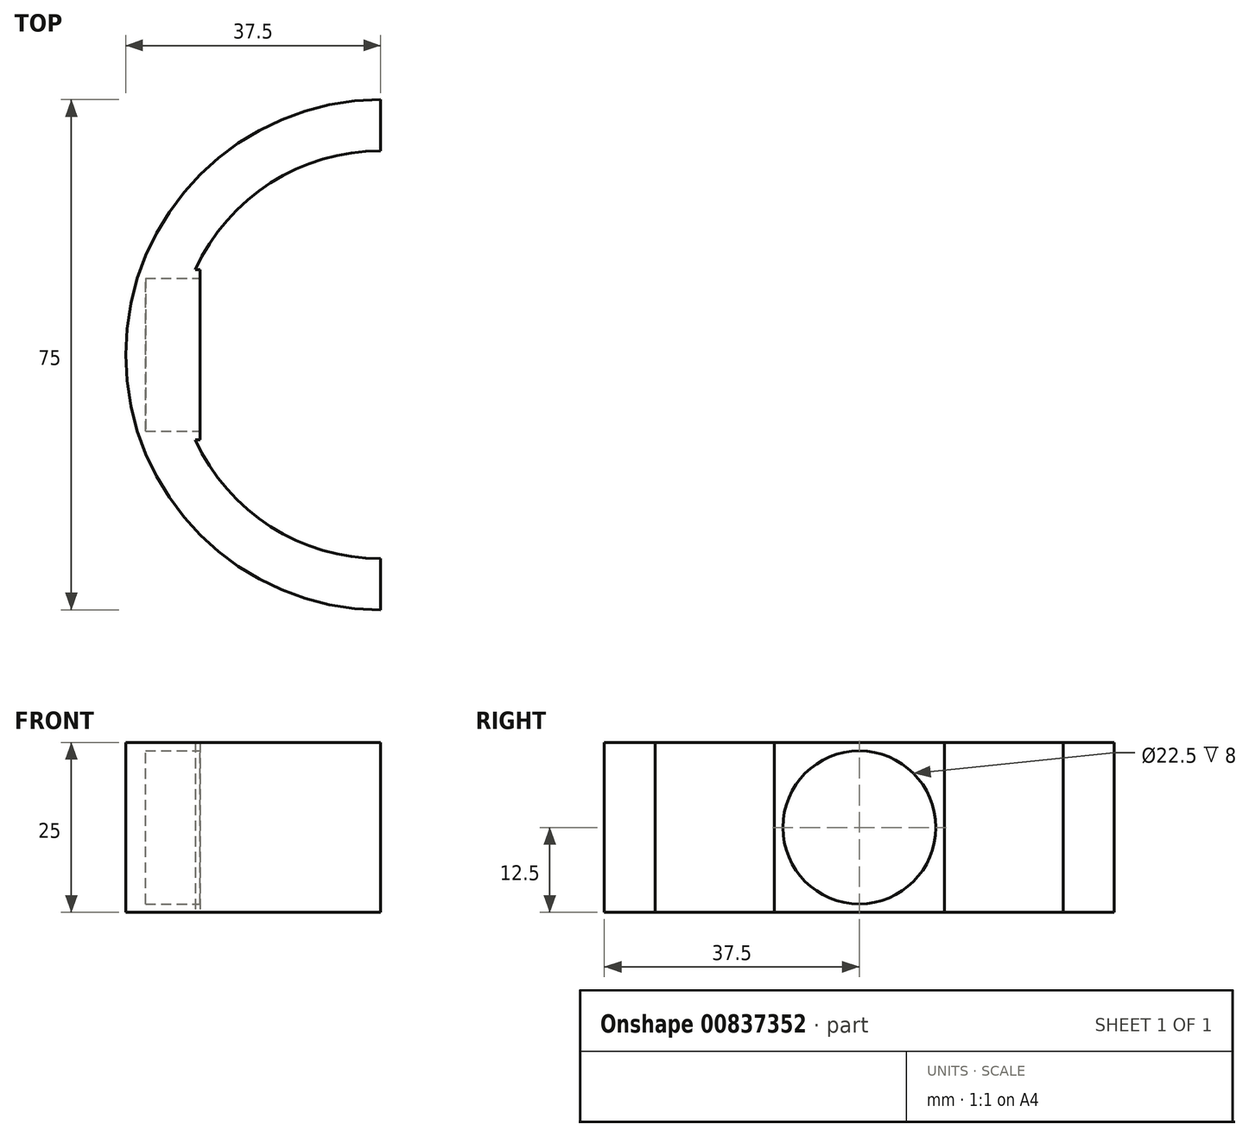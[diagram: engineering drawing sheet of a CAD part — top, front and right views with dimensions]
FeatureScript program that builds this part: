
annotation { "Feature Type Name" : "Feature", "Feature Type Description" : "" }
export const myFeature = defineFeature(function(context is Context, id is Id, definition is map)
    precondition{}
    {
        {
            var Q0;
            Q0=qCreatedBy(makeId("Top.planeOp"),FACE);
            var sketch = newSketch(context, id + "F0", { "sketchPlane" : qUnion([Q0])});
            skArc(sketch, "E0", {"start": v(-27.27, -12.5) * mm, "mid": v(-16.2, -25.25) * mm, "end": v(0, -30) * mm});
            skArc(sketch, "E1", {"start": v(-37.5, 0) * mm, "mid": v(-26.52, -26.52) * mm, "end": v(0, -37.5) * mm});
            skLineSegment(sketch, "E2", {"start": v(-37.5, 0) * mm, "end": v(-26.6, 0) * mm, "construction": true});
            skPoint(sketch, "E2.endSnap0", {"position": v(-26.6, 0) * mm});
            skLineSegment(sketch, "E3", {"start": v(-26.6, -12.5) * mm, "end": v(-27.27, -12.5) * mm});
            skLineSegment(sketch, "E4", {"start": v(0, -30) * mm, "end": v(0, -37.5) * mm});
            skLineSegment(sketch, "E5", {"start": v(-26.6, 0) * mm, "end": v(-26.6, -12.5) * mm});
            skLineSegment(sketch, "E6.MirrorCS", {"start": v(-26.6, 12.5) * mm, "end": v(-27.27, 12.5) * mm});
            skLineSegment(sketch, "E7.MirrorCS", {"start": v(0, 30) * mm, "end": v(0, 37.5) * mm});
            skArc(sketch, "E8.MirrorCS", {"start": v(-37.5, 0) * mm, "mid": v(-26.52, 26.52) * mm, "end": v(0, 37.5) * mm});
            skArc(sketch, "E9.MirrorCS", {"start": v(-27.27, 12.5) * mm, "mid": v(-16.2, 25.25) * mm, "end": v(0, 30) * mm});
            skLineSegment(sketch, "E10.MirrorCS", {"start": v(-26.6, 0) * mm, "end": v(-26.6, 12.5) * mm});
            skSolve(sketch);
        }
        {
            var Q0;
            Q0=makeQuery(id+"F0.imprint","IMPRINT",FACE,{"disambiguationData":[TD([[makeQuery(id+"F0.imprint","IMPRINT",EDGE,{"derivedFrom":sQuery(id+"F0.wireOp",EDGE,"E0")}),-1.0]])]});
            extrude(context, id + "F1", {"entities" : qUnion([Q0]), "depth" : 25 * mm, "offsetDistance" : 25 * mm});
        }
        {
            var Q0;
            Q0=makeQuery(id+"F1.opExtrude","SWEPT_FACE",FACE,{"disambiguationData":[OSD([sQuery(id+"F0.wireOp",EDGE,"E5"),sQuery(id+"F0.wireOp",EDGE,"E10.MirrorCS")])]});
            var sketch = newSketch(context, id + "F2", { "sketchPlane" : qUnion([Q0])});
            skLineSegment(sketch, "E11", {"start": v(-12.5, 25) * mm, "end": v(12.5, 0) * mm, "construction": true});
            skLineSegment(sketch, "E12", {"start": v(-12.5, 0) * mm, "end": v(12.5, 25) * mm, "construction": true});
            skCircle(sketch, "E13", {"center": v(0, 12.5) * mm, "radius": 11.25 * mm});
            skSolve(sketch);
        }
        {
            var Q0;
            Q0=makeQuery(id+"F2.imprint","IMPRINT",FACE,{"disambiguationData":[TD([[makeQuery(id+"F2.imprint","IMPRINT",EDGE,{"derivedFrom":sQuery(id+"F2.wireOp",EDGE,"E13")}),1.0]])]});
            extrude(context, id + "F3", {"entities" : qUnion([Q0]), "operationType" : NewBodyOperationType.REMOVE, "oppositeDirection" : true, "depth" : 8 * mm, "offsetDistance" : 25 * mm});
        }
    });
